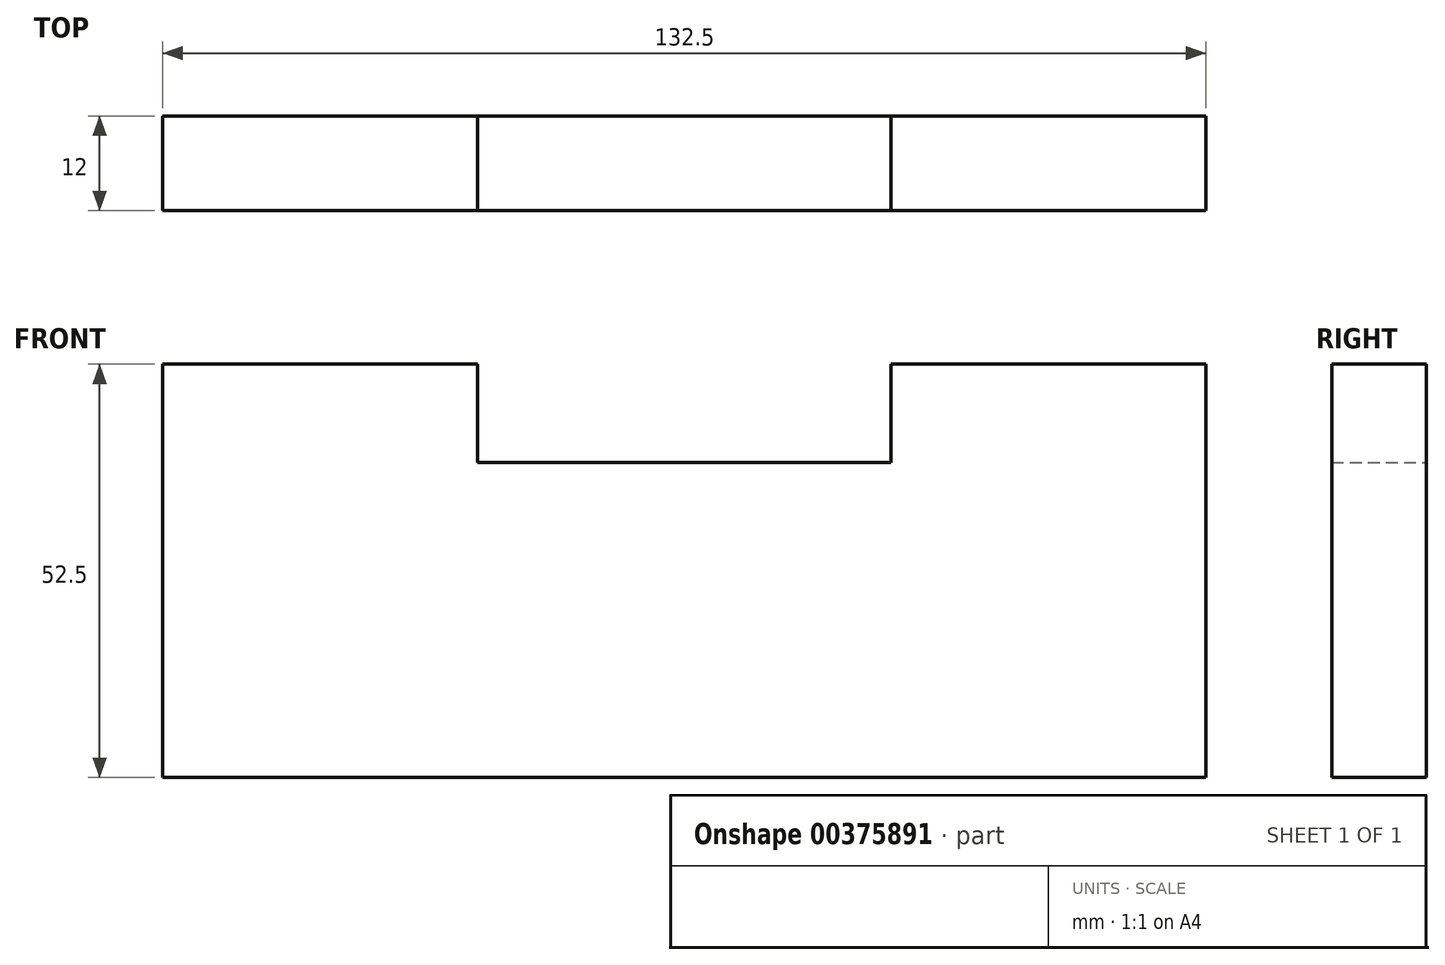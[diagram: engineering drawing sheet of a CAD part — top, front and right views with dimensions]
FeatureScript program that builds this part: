
annotation { "Feature Type Name" : "Feature", "Feature Type Description" : "" }
export const myFeature = defineFeature(function(context is Context, id is Id, definition is map)
    precondition{}
    {
        {
            var Q0;
            Q0=qCreatedBy(makeId("Front.planeOp"),FACE);
            var sketch = newSketch(context, id + "F0", { "sketchPlane" : qUnion([Q0])});
            skLineSegment(sketch, "E0.bottom", {"start": v(-58.47, 37.47) * mm, "end": v(-18.47, 37.47) * mm});
            skLineSegment(sketch, "E0.top", {"start": v(-58.47, -15.03) * mm, "end": v(-18.47, -15.03) * mm});
            skLineSegment(sketch, "E0.left", {"start": v(-58.47, 37.47) * mm, "end": v(-58.47, -15.03) * mm});
            skLineSegment(sketch, "E0.right", {"start": v(-18.47, 37.47) * mm, "end": v(-18.47, -15.03) * mm});
            skLineSegment(sketch, "E1.bottom", {"start": v(-18.47, 24.97) * mm, "end": v(34.03, 24.97) * mm});
            skLineSegment(sketch, "E1.top", {"start": v(-18.47, -15.03) * mm, "end": v(34.03, -15.03) * mm});
            skLineSegment(sketch, "E1.left", {"start": v(-18.47, 24.97) * mm, "end": v(-18.47, -15.03) * mm});
            skLineSegment(sketch, "E1.right", {"start": v(34.03, 24.97) * mm, "end": v(34.03, -15.03) * mm});
            skLineSegment(sketch, "E2.bottom", {"start": v(34.03, 37.47) * mm, "end": v(74.03, 37.47) * mm});
            skLineSegment(sketch, "E2.top", {"start": v(34.03, -15.03) * mm, "end": v(74.03, -15.03) * mm});
            skLineSegment(sketch, "E2.left", {"start": v(34.03, 37.47) * mm, "end": v(34.03, -15.03) * mm});
            skLineSegment(sketch, "E2.right", {"start": v(74.03, 37.47) * mm, "end": v(74.03, -15.03) * mm});
            skSolve(sketch);
        }
        {
            var Q0;
            Q0 = qSketchRegion(id + "F0", true);
            extrude(context, id + "F1", {"entities" : qUnion([Q0]), "depth" : 12 * mm});
        }
    });
